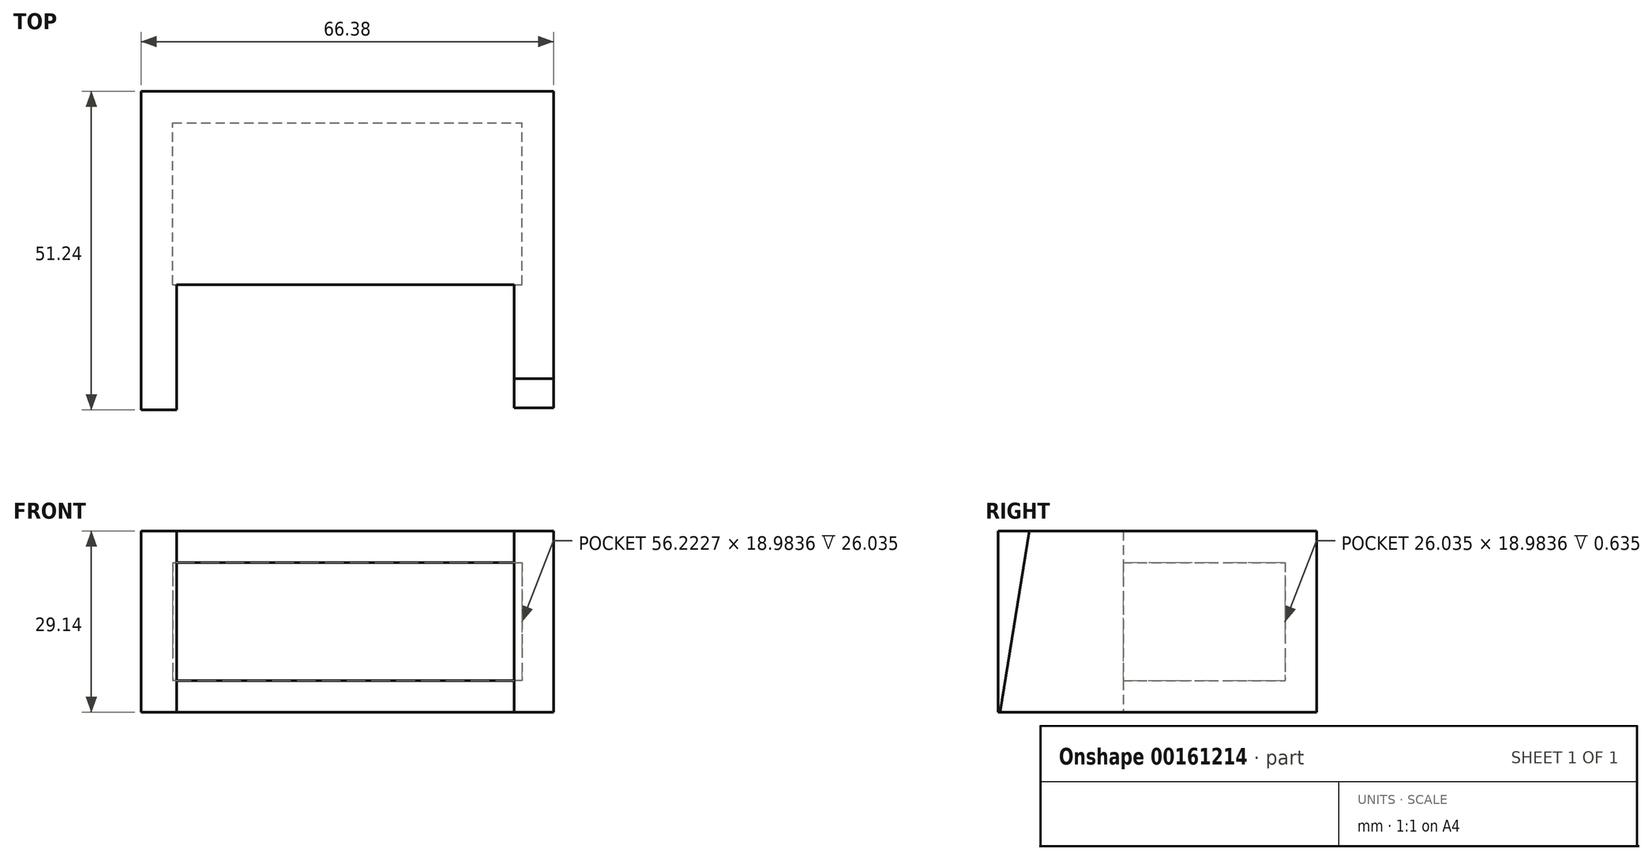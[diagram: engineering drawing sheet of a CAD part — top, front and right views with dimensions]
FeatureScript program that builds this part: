
annotation { "Feature Type Name" : "Feature", "Feature Type Description" : "" }
export const myFeature = defineFeature(function(context is Context, id is Id, definition is map)
    precondition{}
    {
        {
            var Q0;
            Q0=qCreatedBy(makeId("Front.planeOp"),FACE);
            var sketch = newSketch(context, id + "F0", { "sketchPlane" : qUnion([Q0])});
            skLineSegment(sketch, "E0", {"start": v(-37.78, 19.02) * mm, "end": v(28.6, 19.02) * mm});
            skLineSegment(sketch, "E1", {"start": v(28.6, 19.02) * mm, "end": v(28.6, -10.12) * mm});
            skLineSegment(sketch, "E2", {"start": v(-37.78, 19.02) * mm, "end": v(-37.78, -10.12) * mm});
            skLineSegment(sketch, "E3", {"start": v(28.6, -10.12) * mm, "end": v(-37.78, -10.12) * mm});
            skSolve(sketch);
        }
        {
            var Q0;
            Q0=makeQuery(id+"F0.imprint","IMPRINT",FACE,{"disambiguationData":[TD([[makeQuery(id+"F0.imprint","IMPRINT",EDGE,{"derivedFrom":sQuery(id+"F0.wireOp",EDGE,"E0")}),-1.0]])]});
            extrude(context, id + "F1", {"entities" : qUnion([Q0]), "depth" : 31.1 * mm});
        }
        {
            var Q0;
            Q0=makeQuery(id+"F1.opExtrude","CAP_FACE",FACE,{"disambiguationData":[OSD([sQuery(id+"F0.wireOp",EDGE,"E0"),sQuery(id+"F0.wireOp",EDGE,"E1"),sQuery(id+"F0.wireOp",EDGE,"E2"),sQuery(id+"F0.wireOp",EDGE,"E3")])],"isStart":false});
            shell(context, id + "F2", {"entities" : qUnion([Q0]), "thickness" : 5.08 * mm});
        }
        {
            var Q0;
            Q0=makeQuery(id+"F1.opExtrude","SWEPT_FACE",FACE,{"disambiguationData":[OSD([sQuery(id+"F0.wireOp",EDGE,"E1")])]});
            var sketch = newSketch(context, id + "F3", { "sketchPlane" : qUnion([Q0])});
            skLineSegment(sketch, "E4", {"start": v(-31.12, -10.12) * mm, "end": v(-50.93, -10.12) * mm});
            skLineSegment(sketch, "E5", {"start": v(-31.12, 19.02) * mm, "end": v(-46.24, 19.02) * mm});
            skLineSegment(sketch, "E6", {"start": v(-46.24, 19.02) * mm, "end": v(-50.93, -10.12) * mm});
            skSolve(sketch);
        }
        {
            var Q0;
            Q0=makeQuery(id+"F3.imprint","IMPRINT",FACE,{"disambiguationData":[TD([[makeQuery(id+"F3.imprint","IMPRINT",EDGE,{"derivedFrom":sQuery(id+"F3.wireOp",EDGE,"E4")}),-1.0]])]});
            extrude(context, id + "F4", {"entities" : qUnion([Q0]), "operationType" : NewBodyOperationType.ADD, "oppositeDirection" : true, "depth" : 6.35 * mm});
        }
        {
            var Q0;
            Q0=makeQuery(id+"F1.opExtrude","SWEPT_FACE",FACE,{"disambiguationData":[OSD([sQuery(id+"F0.wireOp",EDGE,"E2")])]});
            var sketch = newSketch(context, id + "F5", { "sketchPlane" : qUnion([Q0])});
            skLineSegment(sketch, "E7", {"start": v(31.12, 19.02) * mm, "end": v(51.24, 19.02) * mm});
            skLineSegment(sketch, "E8", {"start": v(31.12, -10.12) * mm, "end": v(51.24, -10.12) * mm});
            skLineSegment(sketch, "E9", {"start": v(51.24, -10.12) * mm, "end": v(51.24, 19.02) * mm});
            skSolve(sketch);
        }
        {
            var Q0;
            Q0=makeQuery(id+"F5.imprint","IMPRINT",FACE,{"disambiguationData":[TD([[makeQuery(id+"F5.imprint","IMPRINT",EDGE,{"derivedFrom":sQuery(id+"F5.wireOp",EDGE,"E7")}),-1.0]])]});
            extrude(context, id + "F6", {"entities" : qUnion([Q0]), "operationType" : NewBodyOperationType.ADD, "oppositeDirection" : true, "depth" : 5.7 * mm});
        }
    });
